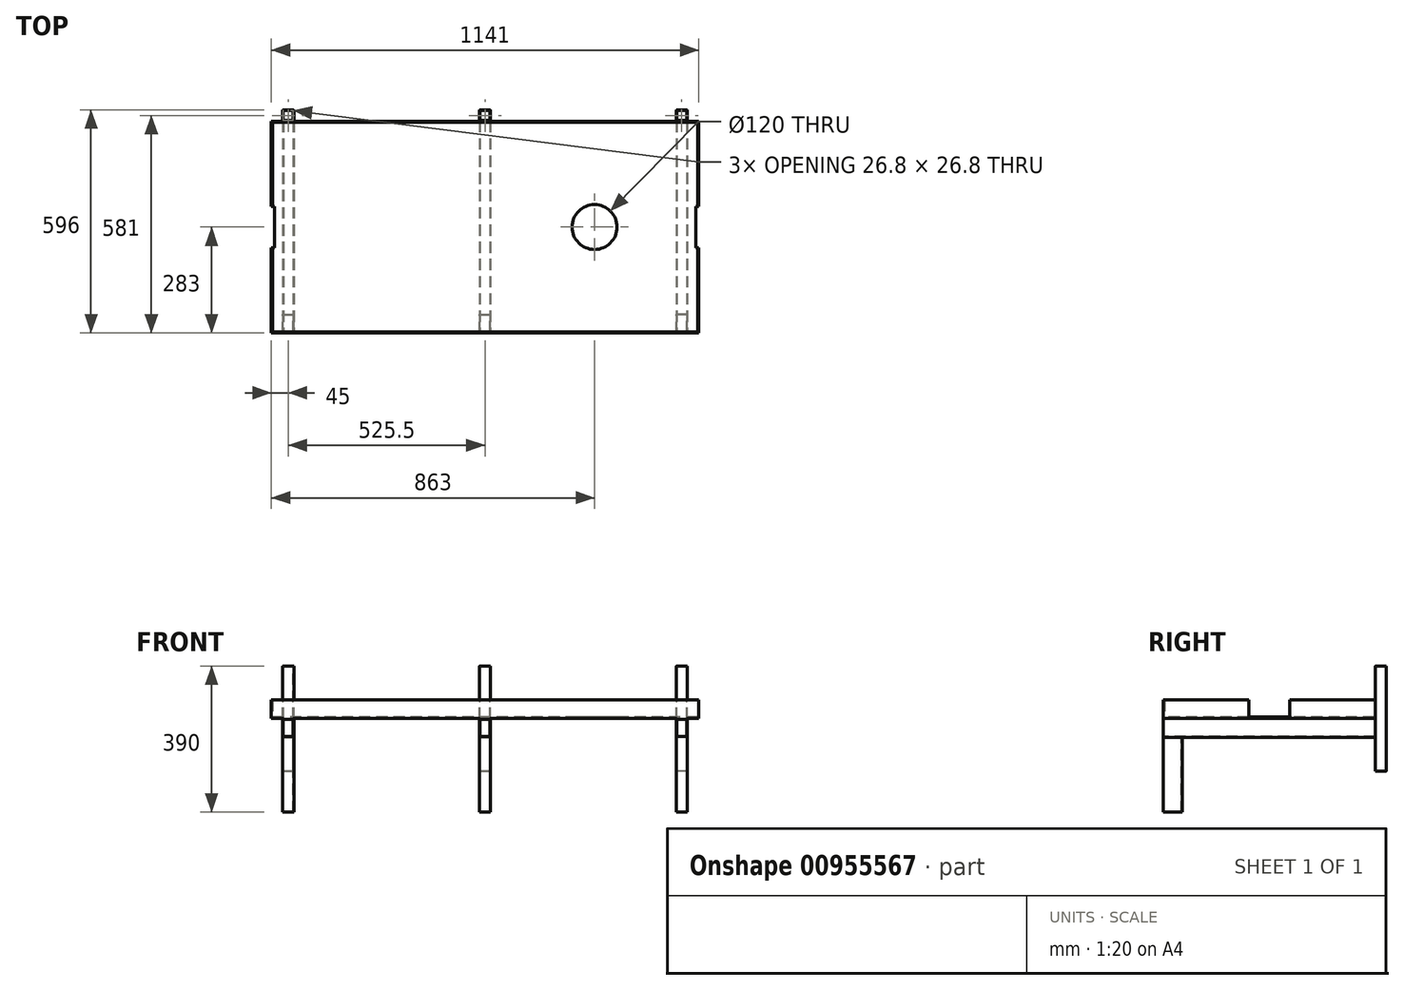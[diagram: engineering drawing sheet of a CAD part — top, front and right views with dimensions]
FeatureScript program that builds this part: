
annotation { "Feature Type Name" : "Feature", "Feature Type Description" : "" }
export const myFeature = defineFeature(function(context is Context, id is Id, definition is map)
    precondition{}
    {
        {
            var Q0;
            Q0=qCreatedBy(makeId("Top.planeOp"),FACE);
            var sketch = newSketch(context, id + "F0", { "sketchPlane" : qUnion([Q0])});
            skLineSegment(sketch, "E0.bottom", {"start": v(567.5, 280) * mm, "end": v(-567.5, 280) * mm});
            skLineSegment(sketch, "E0.top", {"start": v(567.5, -280) * mm, "end": v(-567.5, -280) * mm});
            skLineSegment(sketch, "E0.left", {"start": v(567.5, 280) * mm, "end": v(567.5, -280) * mm});
            skLineSegment(sketch, "E0.right", {"start": v(-567.5, 280) * mm, "end": v(-567.5, -280) * mm});
            skPoint(sketch, "E0.middle", {"position": v(0, 0) * mm});
            skLineSegment(sketch, "E1.0", {"start": v(570.5, 283) * mm, "end": v(-570.5, 283) * mm});
            skLineSegment(sketch, "E1.1", {"start": v(570.5, 283) * mm, "end": v(570.5, -283) * mm});
            skLineSegment(sketch, "E1.2", {"start": v(570.5, -283) * mm, "end": v(-570.5, -283) * mm});
            skLineSegment(sketch, "E1.3", {"start": v(-570.5, 283) * mm, "end": v(-570.5, -283) * mm});
            skLineSegment(sketch, "E2.bottom", {"start": v(567.5, 55) * mm, "end": v(-567.5, 55) * mm, "construction": true});
            skLineSegment(sketch, "E2.top", {"start": v(567.5, -55) * mm, "end": v(-567.5, -55) * mm, "construction": true});
            skLineSegment(sketch, "E2.left", {"start": v(567.5, 55) * mm, "end": v(567.5, -55) * mm, "construction": true});
            skLineSegment(sketch, "E2.right", {"start": v(-567.5, 55) * mm, "end": v(-567.5, -55) * mm, "construction": true});
            skLineSegment(sketch, "E3.bottom", {"start": v(-567.5, -55) * mm, "end": v(-562.5, -55) * mm});
            skLineSegment(sketch, "E3.top", {"start": v(-567.5, 55) * mm, "end": v(-562.5, 55) * mm});
            skLineSegment(sketch, "E3.left", {"start": v(-567.5, -55) * mm, "end": v(-567.5, 55) * mm});
            skLineSegment(sketch, "E3.right", {"start": v(-562.5, -55) * mm, "end": v(-562.5, 55) * mm});
            skLineSegment(sketch, "E4.MirrorCS", {"start": v(562.5, -55) * mm, "end": v(562.5, 55) * mm});
            skLineSegment(sketch, "E5", {"start": v(-567.5, -55) * mm, "end": v(-570.5, -55) * mm});
            skLineSegment(sketch, "E6", {"start": v(-567.5, 55) * mm, "end": v(-570.5, 55) * mm});
            skLineSegment(sketch, "E7.MirrorCS", {"start": v(567.5, -55) * mm, "end": v(570.5, -55) * mm});
            skLineSegment(sketch, "E8.MirrorCS", {"start": v(567.5, 55) * mm, "end": v(570.5, 55) * mm});
            skLineSegment(sketch, "E9", {"start": v(562.5, -55) * mm, "end": v(567.5, -55) * mm});
            skLineSegment(sketch, "E10", {"start": v(562.5, 55) * mm, "end": v(567.5, 55) * mm});
            skLineSegment(sketch, "E11", {"start": v(-567.5, 0) * mm, "end": v(562.5, 0) * mm, "construction": true});
            skCircle(sketch, "E12", {"center": v(292.5, 0) * mm, "radius": 60 * mm});
            skPoint(sketch, "E13", {"position": v(-540.5, 283) * mm});
            skLineSegment(sketch, "E14.bottom", {"start": v(-538.5, 283) * mm, "end": v(-512.5, 283) * mm});
            skLineSegment(sketch, "E14.top", {"start": v(-538.5, 313) * mm, "end": v(-512.5, 313) * mm});
            skLineSegment(sketch, "E14.left", {"start": v(-540.5, 285) * mm, "end": v(-540.5, 311) * mm});
            skLineSegment(sketch, "E14.right", {"start": v(-510.5, 285) * mm, "end": v(-510.5, 311) * mm});
            skLineSegment(sketch, "E15.0", {"start": v(-538.9, 286.6) * mm, "end": v(-538.9, 309.4) * mm});
            skLineSegment(sketch, "E15.1", {"start": v(-536.9, 311.4) * mm, "end": v(-514.1, 311.4) * mm});
            skLineSegment(sketch, "E15.2", {"start": v(-512.1, 286.6) * mm, "end": v(-512.1, 309.4) * mm});
            skLineSegment(sketch, "E16", {"start": v(-536.9, 284.6) * mm, "end": v(-514.1, 284.6) * mm});
            skPoint(sketch, "E17.visualSharp", {"position": v(-538.9, 311.4) * mm});
            skArc(sketch, "E17.filletArc", {"start": v(-536.9, 311.4) * mm, "mid": v(-538.31, 310.81) * mm, "end": v(-538.9, 309.4) * mm});
            skPoint(sketch, "E18.visualSharp", {"position": v(-512.1, 311.4) * mm});
            skArc(sketch, "E18.filletArc", {"start": v(-512.1, 309.4) * mm, "mid": v(-512.69, 310.81) * mm, "end": v(-514.1, 311.4) * mm});
            skPoint(sketch, "E19.visualSharp", {"position": v(-512.1, 284.6) * mm});
            skArc(sketch, "E19.filletArc", {"start": v(-514.1, 284.6) * mm, "mid": v(-512.69, 285.19) * mm, "end": v(-512.1, 286.6) * mm});
            skPoint(sketch, "E20.visualSharp", {"position": v(-538.9, 284.6) * mm});
            skArc(sketch, "E20.filletArc", {"start": v(-538.9, 286.6) * mm, "mid": v(-538.31, 285.19) * mm, "end": v(-536.9, 284.6) * mm});
            skPoint(sketch, "E21.visualSharp", {"position": v(-540.5, 313) * mm});
            skArc(sketch, "E21.filletArc", {"start": v(-538.5, 313) * mm, "mid": v(-539.91, 312.41) * mm, "end": v(-540.5, 311) * mm});
            skPoint(sketch, "E22.visualSharp", {"position": v(-510.5, 313) * mm});
            skArc(sketch, "E22.filletArc", {"start": v(-510.5, 311) * mm, "mid": v(-511.09, 312.41) * mm, "end": v(-512.5, 313) * mm});
            skPoint(sketch, "E23.visualSharp", {"position": v(-510.5, 283) * mm});
            skArc(sketch, "E23.filletArc", {"start": v(-512.5, 283) * mm, "mid": v(-511.09, 283.59) * mm, "end": v(-510.5, 285) * mm});
            skArc(sketch, "E24.filletArc", {"start": v(-540.5, 285) * mm, "mid": v(-539.91, 283.59) * mm, "end": v(-538.5, 283) * mm});
            skLineSegment(sketch, "E25.MirrorCS", {"start": v(538.5, 313) * mm, "end": v(512.5, 313) * mm});
            skLineSegment(sketch, "E26.MirrorCS", {"start": v(536.9, 311.4) * mm, "end": v(514.1, 311.4) * mm});
            skLineSegment(sketch, "E27.MirrorCS", {"start": v(536.9, 284.6) * mm, "end": v(514.1, 284.6) * mm});
            skLineSegment(sketch, "E28.MirrorCS", {"start": v(510.5, 285) * mm, "end": v(510.5, 311) * mm});
            skLineSegment(sketch, "E29.MirrorCS", {"start": v(512.1, 286.6) * mm, "end": v(512.1, 309.4) * mm});
            skLineSegment(sketch, "E30.MirrorCS", {"start": v(538.9, 286.6) * mm, "end": v(538.9, 309.4) * mm});
            skLineSegment(sketch, "E31.MirrorCS", {"start": v(540.5, 285) * mm, "end": v(540.5, 311) * mm});
            skArc(sketch, "E32.MirrorCS", {"start": v(512.1, 309.4) * mm, "mid": v(512.69, 310.81) * mm, "end": v(514.1, 311.4) * mm});
            skArc(sketch, "E33.MirrorCS", {"start": v(510.5, 311) * mm, "mid": v(511.09, 312.41) * mm, "end": v(512.5, 313) * mm});
            skArc(sketch, "E34.MirrorCS", {"start": v(536.9, 311.4) * mm, "mid": v(538.31, 310.81) * mm, "end": v(538.9, 309.4) * mm});
            skArc(sketch, "E35.MirrorCS", {"start": v(538.5, 313) * mm, "mid": v(539.91, 312.41) * mm, "end": v(540.5, 311) * mm});
            skArc(sketch, "E36.MirrorCS", {"start": v(512.5, 283) * mm, "mid": v(511.09, 283.59) * mm, "end": v(510.5, 285) * mm});
            skArc(sketch, "E37.MirrorCS", {"start": v(514.1, 284.6) * mm, "mid": v(512.69, 285.19) * mm, "end": v(512.1, 286.6) * mm});
            skArc(sketch, "E38.MirrorCS", {"start": v(538.9, 286.6) * mm, "mid": v(538.31, 285.19) * mm, "end": v(536.9, 284.6) * mm});
            skArc(sketch, "E39.MirrorCS", {"start": v(540.5, 285) * mm, "mid": v(539.91, 283.59) * mm, "end": v(538.5, 283) * mm});
            skLineSegment(sketch, "E40.1.0.0", {"start": v(-13, 313) * mm, "end": v(13, 313) * mm});
            skPoint(sketch, "E40.1.0.1", {"position": v(-13.4, 284.6) * mm});
            skLineSegment(sketch, "E40.1.0.2", {"start": v(13.4, 286.6) * mm, "end": v(13.4, 309.4) * mm});
            skLineSegment(sketch, "E40.1.0.3", {"start": v(-13.4, 286.6) * mm, "end": v(-13.4, 309.4) * mm});
            skPoint(sketch, "E40.1.0.4", {"position": v(13.4, 284.6) * mm});
            skPoint(sketch, "E40.1.0.5", {"position": v(-15, 313) * mm});
            skLineSegment(sketch, "E40.1.0.6", {"start": v(-15, 285) * mm, "end": v(-15, 311) * mm});
            skPoint(sketch, "E40.1.0.7", {"position": v(13.4, 311.4) * mm});
            skLineSegment(sketch, "E40.1.0.8", {"start": v(-11.4, 284.6) * mm, "end": v(11.4, 284.6) * mm});
            skPoint(sketch, "E40.1.0.9", {"position": v(15, 313) * mm});
            skLineSegment(sketch, "E40.1.0.10", {"start": v(15, 285) * mm, "end": v(15, 311) * mm});
            skLineSegment(sketch, "E40.1.0.11", {"start": v(-13, 283) * mm, "end": v(13, 283) * mm});
            skLineSegment(sketch, "E40.1.0.12", {"start": v(-11.4, 311.4) * mm, "end": v(11.4, 311.4) * mm});
            skPoint(sketch, "E40.1.0.13", {"position": v(-13.4, 311.4) * mm});
            skArc(sketch, "E40.1.0.14", {"start": v(13.4, 309.4) * mm, "mid": v(12.81, 310.81) * mm, "end": v(11.4, 311.4) * mm});
            skArc(sketch, "E40.1.0.15", {"start": v(15, 311) * mm, "mid": v(14.41, 312.41) * mm, "end": v(13, 313) * mm});
            skArc(sketch, "E40.1.0.16", {"start": v(-13, 313) * mm, "mid": v(-14.41, 312.41) * mm, "end": v(-15, 311) * mm});
            skArc(sketch, "E40.1.0.17", {"start": v(-13.4, 286.6) * mm, "mid": v(-12.81, 285.19) * mm, "end": v(-11.4, 284.6) * mm});
            skArc(sketch, "E40.1.0.18", {"start": v(-15, 285) * mm, "mid": v(-14.41, 283.59) * mm, "end": v(-13, 283) * mm});
            skArc(sketch, "E40.1.0.19", {"start": v(11.4, 284.6) * mm, "mid": v(12.81, 285.19) * mm, "end": v(13.4, 286.6) * mm});
            skArc(sketch, "E40.1.0.20", {"start": v(-11.4, 311.4) * mm, "mid": v(-12.81, 310.81) * mm, "end": v(-13.4, 309.4) * mm});
            skArc(sketch, "E40.1.0.21", {"start": v(13, 283) * mm, "mid": v(14.41, 283.59) * mm, "end": v(15, 285) * mm});
            skLineSegment(sketch, "E40.direction1", {"start": v(-538.5, 283) * mm, "end": v(-13, 283) * mm, "construction": true});
            skPoint(sketch, "E41", {"position": v(525.5, 284.6) * mm});
            skLineSegment(sketch, "E42.bottom", {"start": v(-540.5, 313) * mm, "end": v(-510.5, 313) * mm});
            skLineSegment(sketch, "E42.top", {"start": v(-540.5, 333) * mm, "end": v(-510.5, 333) * mm});
            skLineSegment(sketch, "E42.left", {"start": v(-540.5, 313) * mm, "end": v(-540.5, 333) * mm});
            skLineSegment(sketch, "E42.right", {"start": v(-510.5, 313) * mm, "end": v(-510.5, 333) * mm});
            skLineSegment(sketch, "E43.MirrorCS", {"start": v(540.5, 333) * mm, "end": v(510.5, 333) * mm});
            skLineSegment(sketch, "E44.MirrorCS", {"start": v(510.5, 313) * mm, "end": v(510.5, 333) * mm});
            skLineSegment(sketch, "E45.MirrorCS", {"start": v(540.5, 313) * mm, "end": v(540.5, 333) * mm});
            skLineSegment(sketch, "E46.MirrorCS", {"start": v(540.5, 313) * mm, "end": v(510.5, 313) * mm});
            skLineSegment(sketch, "E47.bottom", {"start": v(-15, 313) * mm, "end": v(15, 313) * mm});
            skLineSegment(sketch, "E47.top", {"start": v(-15, 333) * mm, "end": v(15, 333) * mm});
            skLineSegment(sketch, "E47.left", {"start": v(-15, 313) * mm, "end": v(-15, 333) * mm});
            skLineSegment(sketch, "E47.right", {"start": v(15, 313) * mm, "end": v(15, 333) * mm});
            skSolve(sketch);
        }
        {
            var Q0;
            {var subQ3=sQuery(id+"F0.wireOp",EDGE,"E0.bottom");Q0=makeQuery(id+"F0.imprint","IMPRINT",FACE,{"disambiguationData":[TD([[makeQuery(id+"F0.imprint","IMPRINT",EDGE,{"derivedFrom":subQ3}),1.0]])]});}
            extrude(context, id + "F1", {"entities" : qUnion([Q0]), "depth" : 4 * mm, "offsetDistance" : 25 * mm});
        }
        {
            var Q0;
            {var subQ10=sQuery(id+"F0.wireOp",EDGE,"E0.bottom");Q0=makeQuery(id+"F0.imprint","IMPRINT",FACE,{"disambiguationData":[TD([[makeQuery(id+"F0.imprint","IMPRINT",EDGE,{"derivedFrom":subQ10}),-1.0]])]});}
            var Q1;
            {var subQ1=sQuery(id+"F0.wireOp",EDGE,"E0.top");Q1=makeQuery(id+"F0.imprint","IMPRINT",FACE,{"disambiguationData":[TD([[makeQuery(id+"F0.imprint","IMPRINT",EDGE,{"derivedFrom":subQ1}),1.0]])]});}
            extrude(context, id + "F2", {"entities" : qUnion([Q0, Q1]), "operationType" : NewBodyOperationType.ADD, "depth" : 50 * mm, "offsetDistance" : 25 * mm});
        }
        {
            var Q0;
            Q0=makeQuery(id+"F2.opExtrude","SWEPT_FACE",FACE,{"disambiguationData":[OSD([sQuery(id+"F0.wireOp",EDGE,"E1.2")])]});
            var sketch = newSketch(context, id + "F3", { "sketchPlane" : qUnion([Q0])});
            skPoint(sketch, "E48", {"position": v(-540.5, 0) * mm});
            skLineSegment(sketch, "E49.bottom", {"start": v(-538.5, 0) * mm, "end": v(-512.5, 0) * mm});
            skLineSegment(sketch, "E49.top", {"start": v(-538.5, -50) * mm, "end": v(-512.5, -50) * mm});
            skLineSegment(sketch, "E49.left", {"start": v(-540.5, -2) * mm, "end": v(-540.5, -48) * mm});
            skLineSegment(sketch, "E49.right", {"start": v(-510.5, -2) * mm, "end": v(-510.5, -48) * mm});
            skLineSegment(sketch, "E50.MirrorCS", {"start": v(538.5, -50) * mm, "end": v(512.5, -50) * mm});
            skLineSegment(sketch, "E51.MirrorCS", {"start": v(540.5, -2) * mm, "end": v(540.5, -48) * mm});
            skLineSegment(sketch, "E52.MirrorCS", {"start": v(510.5, -2) * mm, "end": v(510.5, -48) * mm});
            skLineSegment(sketch, "E53.MirrorCS", {"start": v(538.5, 0) * mm, "end": v(512.5, 0) * mm});
            skPoint(sketch, "E54", {"position": v(-15, 0) * mm});
            skLineSegment(sketch, "E55.bottom", {"start": v(-13, 0) * mm, "end": v(13, 0) * mm});
            skLineSegment(sketch, "E55.top", {"start": v(-13, -50) * mm, "end": v(13, -50) * mm});
            skLineSegment(sketch, "E55.left", {"start": v(-15, -2) * mm, "end": v(-15, -48) * mm});
            skLineSegment(sketch, "E55.right", {"start": v(15, -2) * mm, "end": v(15, -48) * mm});
            skPoint(sketch, "E56.visualSharp", {"position": v(-510.5, -50) * mm});
            skArc(sketch, "E56.filletArc", {"start": v(-512.5, -50) * mm, "mid": v(-511.09, -49.41) * mm, "end": v(-510.5, -48) * mm});
            skPoint(sketch, "E57.visualSharp", {"position": v(-540.5, -50) * mm});
            skArc(sketch, "E57.filletArc", {"start": v(-540.5, -48) * mm, "mid": v(-539.91, -49.41) * mm, "end": v(-538.5, -50) * mm});
            skPoint(sketch, "E58.visualSharp", {"position": v(-510.5, 0) * mm});
            skArc(sketch, "E58.filletArc", {"start": v(-510.5, -2) * mm, "mid": v(-511.09, -0.59) * mm, "end": v(-512.5, 0) * mm});
            skArc(sketch, "E59.filletArc", {"start": v(-538.5, 0) * mm, "mid": v(-539.91, -0.59) * mm, "end": v(-540.5, -2) * mm});
            skPoint(sketch, "E60.visualSharp", {"position": v(540.5, 0) * mm});
            skArc(sketch, "E60.filletArc", {"start": v(540.5, -2) * mm, "mid": v(539.91, -0.59) * mm, "end": v(538.5, 0) * mm});
            skPoint(sketch, "E61.visualSharp", {"position": v(510.5, 0) * mm});
            skArc(sketch, "E61.filletArc", {"start": v(512.5, 0) * mm, "mid": v(511.09, -0.59) * mm, "end": v(510.5, -2) * mm});
            skPoint(sketch, "E62.visualSharp", {"position": v(510.5, -50) * mm});
            skArc(sketch, "E62.filletArc", {"start": v(510.5, -48) * mm, "mid": v(511.09, -49.41) * mm, "end": v(512.5, -50) * mm});
            skPoint(sketch, "E63.visualSharp", {"position": v(540.5, -50) * mm});
            skArc(sketch, "E63.filletArc", {"start": v(538.5, -50) * mm, "mid": v(539.91, -49.41) * mm, "end": v(540.5, -48) * mm});
            skPoint(sketch, "E64.visualSharp", {"position": v(-15, -50) * mm});
            skArc(sketch, "E64.filletArc", {"start": v(-15, -48) * mm, "mid": v(-14.41, -49.41) * mm, "end": v(-13, -50) * mm});
            skPoint(sketch, "E65.visualSharp", {"position": v(15, -50) * mm});
            skArc(sketch, "E65.filletArc", {"start": v(13, -50) * mm, "mid": v(14.41, -49.41) * mm, "end": v(15, -48) * mm});
            skPoint(sketch, "E66.visualSharp", {"position": v(15, 0) * mm});
            skArc(sketch, "E66.filletArc", {"start": v(15, -2) * mm, "mid": v(14.41, -0.59) * mm, "end": v(13, 0) * mm});
            skArc(sketch, "E67.filletArc", {"start": v(-13, 0) * mm, "mid": v(-14.41, -0.59) * mm, "end": v(-15, -2) * mm});
            skLineSegment(sketch, "E68.0", {"start": v(-538.9, -2) * mm, "end": v(-538.9, -48) * mm});
            skArc(sketch, "E69.0", {"start": v(-538.9, -48) * mm, "mid": v(-538.78, -48.28) * mm, "end": v(-538.5, -48.4) * mm});
            skLineSegment(sketch, "E70.0", {"start": v(-538.5, -48.4) * mm, "end": v(-512.5, -48.4) * mm});
            skArc(sketch, "E71.0", {"start": v(-512.5, -48.4) * mm, "mid": v(-512.22, -48.28) * mm, "end": v(-512.1, -48) * mm});
            skLineSegment(sketch, "E72.0", {"start": v(-512.1, -2) * mm, "end": v(-512.1, -48) * mm});
            skArc(sketch, "E73.0", {"start": v(-512.1, -2) * mm, "mid": v(-512.22, -1.72) * mm, "end": v(-512.5, -1.6) * mm});
            skArc(sketch, "E74.0", {"start": v(-538.5, -1.6) * mm, "mid": v(-538.78, -1.72) * mm, "end": v(-538.9, -2) * mm});
            skLineSegment(sketch, "E75.0", {"start": v(-538.5, -1.6) * mm, "end": v(-512.5, -1.6) * mm});
            skLineSegment(sketch, "E76.MirrorCS", {"start": v(538.5, -48.4) * mm, "end": v(512.5, -48.4) * mm});
            skArc(sketch, "E77.MirrorCS", {"start": v(538.9, -48) * mm, "mid": v(538.78, -48.28) * mm, "end": v(538.5, -48.4) * mm});
            skLineSegment(sketch, "E78.MirrorCS", {"start": v(538.9, -2) * mm, "end": v(538.9, -48) * mm});
            skArc(sketch, "E79.MirrorCS", {"start": v(512.5, -48.4) * mm, "mid": v(512.22, -48.28) * mm, "end": v(512.1, -48) * mm});
            skLineSegment(sketch, "E80.MirrorCS", {"start": v(512.1, -2) * mm, "end": v(512.1, -48) * mm});
            skArc(sketch, "E81.MirrorCS", {"start": v(512.1, -2) * mm, "mid": v(512.22, -1.72) * mm, "end": v(512.5, -1.6) * mm});
            skLineSegment(sketch, "E82.MirrorCS", {"start": v(538.5, -1.6) * mm, "end": v(512.5, -1.6) * mm});
            skArc(sketch, "E83.MirrorCS", {"start": v(538.5, -1.6) * mm, "mid": v(538.78, -1.72) * mm, "end": v(538.9, -2) * mm});
            skLineSegment(sketch, "E84.0", {"start": v(-13.4, -2) * mm, "end": v(-13.4, -48) * mm});
            skLineSegment(sketch, "E85.0", {"start": v(-13, -1.6) * mm, "end": v(13, -1.6) * mm});
            skLineSegment(sketch, "E86.0", {"start": v(13.4, -2) * mm, "end": v(13.4, -48) * mm});
            skLineSegment(sketch, "E87.0", {"start": v(-13, -48.4) * mm, "end": v(13, -48.4) * mm});
            skArc(sketch, "E88.0", {"start": v(-13.4, -48) * mm, "mid": v(-13.28, -48.28) * mm, "end": v(-13, -48.4) * mm});
            skArc(sketch, "E89.0", {"start": v(13, -48.4) * mm, "mid": v(13.28, -48.28) * mm, "end": v(13.4, -48) * mm});
            skArc(sketch, "E90.0", {"start": v(13.4, -2) * mm, "mid": v(13.28, -1.72) * mm, "end": v(13, -1.6) * mm});
            skArc(sketch, "E91.0", {"start": v(-13, -1.6) * mm, "mid": v(-13.28, -1.72) * mm, "end": v(-13.4, -2) * mm});
            skSolve(sketch);
        }
        {
            var Q0;
            Q0=makeQuery(id+"F3.imprint","IMPRINT",FACE,{"disambiguationData":[TD([[makeQuery(id+"F3.imprint","IMPRINT",EDGE,{"derivedFrom":sQuery(id+"F3.wireOp",EDGE,"E49.bottom")}),1.0]])]});
            var Q1;
            Q1=makeQuery(id+"F3.imprint","IMPRINT",FACE,{"disambiguationData":[TD([[makeQuery(id+"F3.imprint","IMPRINT",EDGE,{"derivedFrom":sQuery(id+"F3.wireOp",EDGE,"E55.bottom")}),1.0]])]});
            var Q2;
            Q2=makeQuery(id+"F3.imprint","IMPRINT",FACE,{"disambiguationData":[TD([[makeQuery(id+"F3.imprint","IMPRINT",EDGE,{"derivedFrom":sQuery(id+"F3.wireOp",EDGE,"E50.MirrorCS")}),-1.0]])]});
            extrude(context, id + "F4", {"entities" : qUnion([Q0, Q1, Q2]), "operationType" : NewBodyOperationType.ADD, "oppositeDirection" : true, "depth" : 566 * mm, "offsetDistance" : 25 * mm});
        }
        {
            var Q0;
            Q0=makeQuery(id+"F0.imprint","IMPRINT",FACE,{"disambiguationData":[TD([[makeQuery(id+"F0.imprint","IMPRINT",EDGE,{"derivedFrom":sQuery(id+"F0.wireOp",EDGE,"E14.top")}),-1.0]])]});
            var Q1;
            Q1=makeQuery(id+"F0.imprint","IMPRINT",FACE,{"disambiguationData":[TD([[makeQuery(id+"F0.imprint","IMPRINT",EDGE,{"derivedFrom":sQuery(id+"F0.wireOp",EDGE,"E40.1.0.0")}),-1.0]])]});
            var Q2;
            Q2=makeQuery(id+"F0.imprint","IMPRINT",FACE,{"disambiguationData":[TD([[makeQuery(id+"F0.imprint","IMPRINT",EDGE,{"derivedFrom":sQuery(id+"F0.wireOp",EDGE,"E25.MirrorCS")}),1.0]])]});
            extrude(context, id + "F5", {"entities" : qUnion([Q0, Q1, Q2]), "operationType" : NewBodyOperationType.ADD, "oppositeDirection" : true, "depth" : 140 * mm, "offsetDistance" : 25 * mm, "hasSecondDirection" : true, "secondDirectionOppositeDirection" : false, "secondDirectionDepth" : 140 * mm});
        }
        {
            var Q0;
            Q0=makeQuery(id+"F4.opExtrude","SWEPT_FACE",FACE,{"disambiguationData":[OSD([sQuery(id+"F3.wireOp",EDGE,"E55.top")])]});
            var sketch = newSketch(context, id + "F6", { "sketchPlane" : qUnion([Q0])});
            skPoint(sketch, "E92", {"position": v(-15, 283) * mm});
            skLineSegment(sketch, "E93.bottom", {"start": v(-15, 283) * mm, "end": v(15, 283) * mm});
            skLineSegment(sketch, "E93.top", {"start": v(-15, 233) * mm, "end": v(15, 233) * mm});
            skLineSegment(sketch, "E93.left", {"start": v(-15, 283) * mm, "end": v(-15, 233) * mm});
            skLineSegment(sketch, "E93.right", {"start": v(15, 283) * mm, "end": v(15, 233) * mm});
            skPoint(sketch, "E94", {"position": v(-540.5, 283) * mm});
            skLineSegment(sketch, "E95.bottom", {"start": v(-540.5, 283) * mm, "end": v(-510.5, 283) * mm});
            skLineSegment(sketch, "E95.top", {"start": v(-540.5, 233) * mm, "end": v(-510.5, 233) * mm});
            skLineSegment(sketch, "E95.left", {"start": v(-540.5, 283) * mm, "end": v(-540.5, 233) * mm});
            skLineSegment(sketch, "E95.right", {"start": v(-510.5, 283) * mm, "end": v(-510.5, 233) * mm});
            skLineSegment(sketch, "E96.MirrorCS", {"start": v(540.5, 283) * mm, "end": v(510.5, 283) * mm});
            skLineSegment(sketch, "E97.MirrorCS", {"start": v(540.5, 283) * mm, "end": v(540.5, 233) * mm});
            skLineSegment(sketch, "E98.MirrorCS", {"start": v(540.5, 233) * mm, "end": v(510.5, 233) * mm});
            skLineSegment(sketch, "E99.MirrorCS", {"start": v(510.5, 283) * mm, "end": v(510.5, 233) * mm});
            skLineSegment(sketch, "E100.0", {"start": v(-538.9, 234.6) * mm, "end": v(-512.1, 234.6) * mm});
            skLineSegment(sketch, "E100.1", {"start": v(-538.9, 281.4) * mm, "end": v(-538.9, 234.6) * mm});
            skLineSegment(sketch, "E100.2", {"start": v(-538.9, 281.4) * mm, "end": v(-512.1, 281.4) * mm});
            skLineSegment(sketch, "E100.3", {"start": v(-512.1, 281.4) * mm, "end": v(-512.1, 234.6) * mm});
            skLineSegment(sketch, "E101.0", {"start": v(13.4, 281.4) * mm, "end": v(13.4, 234.6) * mm});
            skLineSegment(sketch, "E101.1", {"start": v(-13.4, 281.4) * mm, "end": v(13.4, 281.4) * mm});
            skLineSegment(sketch, "E101.2", {"start": v(-13.4, 281.4) * mm, "end": v(-13.4, 234.6) * mm});
            skLineSegment(sketch, "E101.3", {"start": v(-13.4, 234.6) * mm, "end": v(13.4, 234.6) * mm});
            skLineSegment(sketch, "E102.0", {"start": v(538.9, 234.6) * mm, "end": v(512.1, 234.6) * mm});
            skLineSegment(sketch, "E102.1", {"start": v(538.9, 281.4) * mm, "end": v(538.9, 234.6) * mm});
            skLineSegment(sketch, "E102.2", {"start": v(538.9, 281.4) * mm, "end": v(512.1, 281.4) * mm});
            skLineSegment(sketch, "E102.3", {"start": v(512.1, 281.4) * mm, "end": v(512.1, 234.6) * mm});
            skSolve(sketch);
        }
        {
            var Q0;
            Q0 = qSketchRegion(id + "F6", true);
            extrude(context, id + "F7", {"entities" : qUnion([Q0]), "operationType" : NewBodyOperationType.ADD, "depth" : 200 * mm, "offsetDistance" : 25 * mm});
        }
    });
